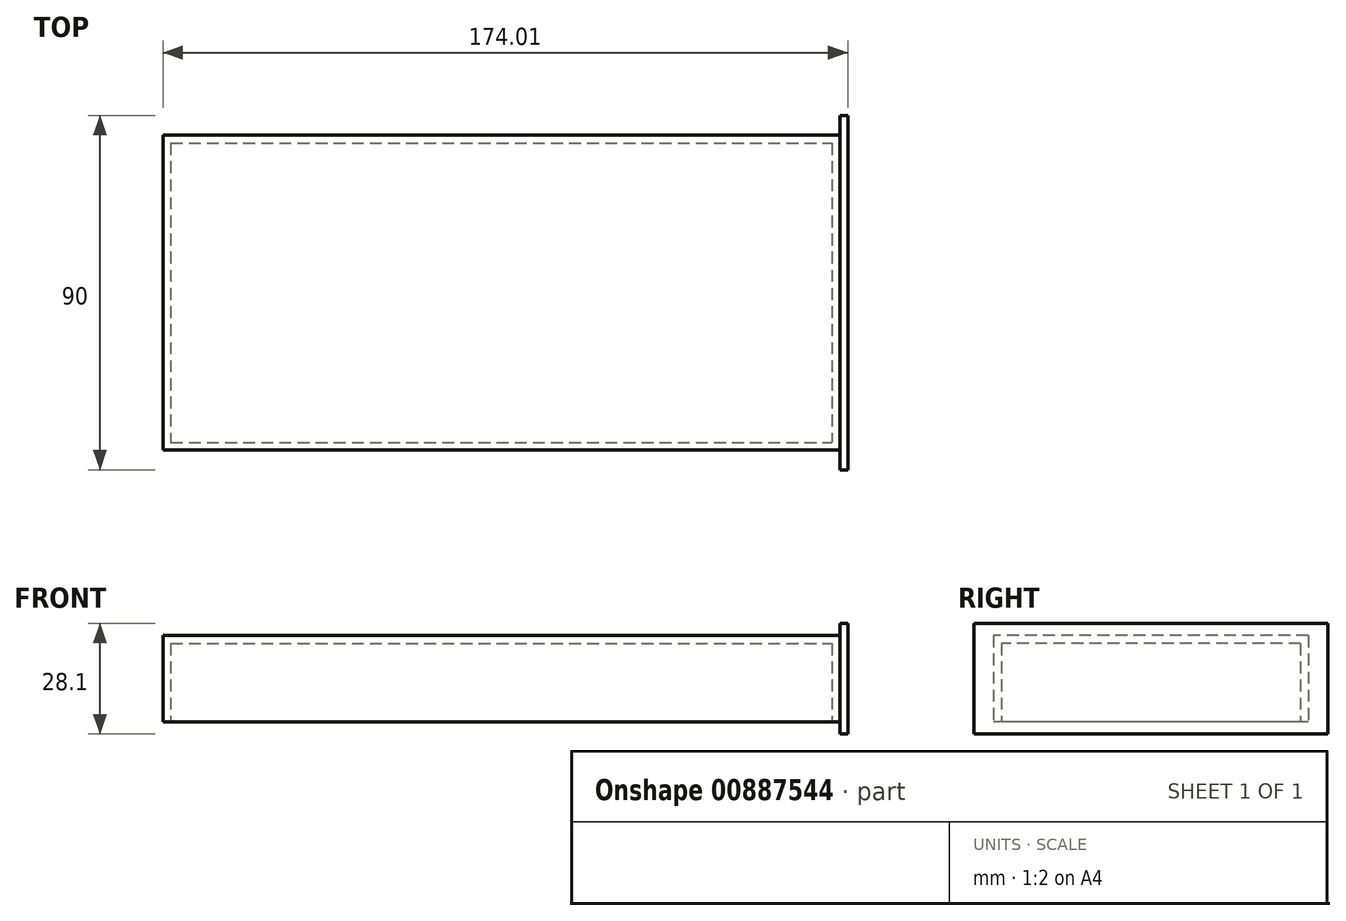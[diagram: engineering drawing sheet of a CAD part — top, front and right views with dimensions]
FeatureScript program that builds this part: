
annotation { "Feature Type Name" : "Feature", "Feature Type Description" : "" }
export const myFeature = defineFeature(function(context is Context, id is Id, definition is map)
    precondition{}
    {
        {
            var Q0;
            Q0=qCreatedBy(makeId("Top.planeOp"),FACE);
            var sketch = newSketch(context, id + "F0", { "sketchPlane" : qUnion([Q0])});
            skLineSegment(sketch, "E0.bottom", {"start": v(-83.22, 31.58) * mm, "end": v(88.78, 31.58) * mm});
            skLineSegment(sketch, "E0.top", {"start": v(-83.22, -48.42) * mm, "end": v(88.78, -48.42) * mm});
            skLineSegment(sketch, "E0.left", {"start": v(-83.22, 31.58) * mm, "end": v(-83.22, -48.42) * mm});
            skLineSegment(sketch, "E0.right", {"start": v(88.78, 31.58) * mm, "end": v(88.78, -48.42) * mm});
            skSolve(sketch);
        }
        {
            var Q0;
            Q0=makeQuery(id+"F0.imprint","IMPRINT",FACE,{"disambiguationData":[TD([[makeQuery(id+"F0.imprint","IMPRINT",EDGE,{"derivedFrom":sQuery(id+"F0.wireOp",EDGE,"E0.bottom")}),-1.0]])]});
            extrude(context, id + "F1", {"entities" : qUnion([Q0]), "depth" : 22 * mm, "offsetDistance" : 25 * mm});
        }
        {
            var Q0;
            Q0=makeQuery(id+"F1.opExtrude","CAP_FACE",FACE,{"disambiguationData":[OSD([sQuery(id+"F0.wireOp",EDGE,"E0.bottom"),sQuery(id+"F0.wireOp",EDGE,"E0.top"),sQuery(id+"F0.wireOp",EDGE,"E0.left"),sQuery(id+"F0.wireOp",EDGE,"E0.right")])],"isStart":true});
            shell(context, id + "F2", {"entities" : qUnion([Q0]), "thickness" : 2 * mm});
        }
        {
            var Q0;
            Q0=qCreatedBy(makeId("Top.planeOp"),FACE);
            var sketch = newSketch(context, id + "F3", { "sketchPlane" : qUnion([Q0])});
            skLineSegment(sketch, "E1", {"start": v(88.79, -53.42) * mm, "end": v(88.79, 36.58) * mm});
            skLineSegment(sketch, "E2", {"start": v(88.79, 36.58) * mm, "end": v(90.79, 36.58) * mm});
            skLineSegment(sketch, "E3", {"start": v(90.79, -53.42) * mm, "end": v(88.79, -53.42) * mm});
            skLineSegment(sketch, "E4", {"start": v(90.79, 36.58) * mm, "end": v(90.79, -53.42) * mm});
            skSolve(sketch);
        }
        {
            var Q0;
            Q0=makeQuery(id+"F3.imprint","IMPRINT",FACE,{"disambiguationData":[TD([[makeQuery(id+"F3.imprint","IMPRINT",EDGE,{"derivedFrom":sQuery(id+"F3.wireOp",EDGE,"E1")}),-1.0]])]});
            extrude(context, id + "F4", {"entities" : qUnion([Q0]), "depth" : 22.1 * mm, "offsetDistance" : 25 * mm});
        }
        {
            var Q0;
            Q0=makeQuery(id+"F4.opExtrude","CAP_FACE",FACE,{"disambiguationData":[OSD([sQuery(id+"F3.wireOp",EDGE,"E1"),sQuery(id+"F3.wireOp",EDGE,"E2"),sQuery(id+"F3.wireOp",EDGE,"E3"),sQuery(id+"F3.wireOp",EDGE,"E4")])],"isStart":true});
            extrude(context, id + "F5", {"entities" : qUnion([Q0]), "operationType" : NewBodyOperationType.ADD, "depth" : 3 * mm, "offsetDistance" : 25 * mm});
        }
        {
            var Q0;
            Q0=makeQuery(id+"F4.opExtrude","CAP_FACE",FACE,{"disambiguationData":[OSD([sQuery(id+"F3.wireOp",EDGE,"E1"),sQuery(id+"F3.wireOp",EDGE,"E2"),sQuery(id+"F3.wireOp",EDGE,"E3"),sQuery(id+"F3.wireOp",EDGE,"E4")])],"isStart":false});
            extrude(context, id + "F6", {"entities" : qUnion([Q0]), "operationType" : NewBodyOperationType.ADD, "depth" : 3 * mm, "offsetDistance" : 25 * mm});
        }
    });
